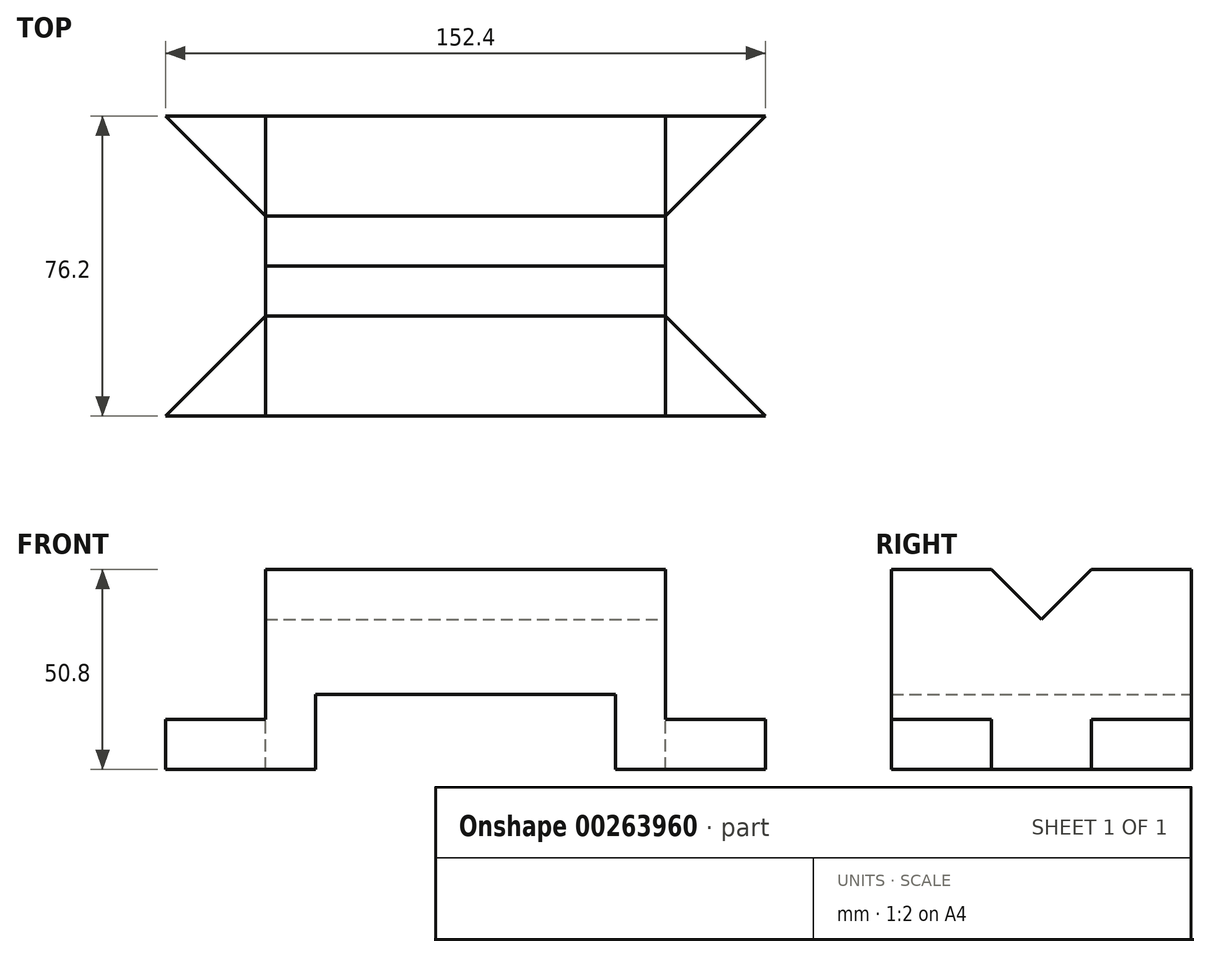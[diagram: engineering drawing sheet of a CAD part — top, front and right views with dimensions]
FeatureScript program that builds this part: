
annotation { "Feature Type Name" : "Feature", "Feature Type Description" : "" }
export const myFeature = defineFeature(function(context is Context, id is Id, definition is map)
    precondition{}
    {
        {
            var Q0;
            Q0=qCreatedBy(makeId("Front.planeOp"),FACE);
            var sketch = newSketch(context, id + "F0", { "sketchPlane" : qUnion([Q0])});
            skLineSegment(sketch, "E0", {"start": v(0, 0) * mm, "end": v(38.1, 0) * mm});
            skLineSegment(sketch, "E1", {"start": v(38.1, 0) * mm, "end": v(38.1, 19.05) * mm});
            skLineSegment(sketch, "E2", {"start": v(38.1, 19.05) * mm, "end": v(114.3, 19.05) * mm});
            skLineSegment(sketch, "E3", {"start": v(114.3, 19.05) * mm, "end": v(114.3, 0) * mm});
            skLineSegment(sketch, "E4", {"start": v(114.3, 0) * mm, "end": v(152.4, 0) * mm});
            skLineSegment(sketch, "E5", {"start": v(152.4, 0) * mm, "end": v(152.4, 12.7) * mm});
            skLineSegment(sketch, "E6", {"start": v(152.4, 12.7) * mm, "end": v(127, 12.7) * mm});
            skLineSegment(sketch, "E7", {"start": v(127, 12.7) * mm, "end": v(127, 50.8) * mm});
            skLineSegment(sketch, "E8", {"start": v(127, 50.8) * mm, "end": v(25.4, 50.8) * mm});
            skLineSegment(sketch, "E9", {"start": v(25.4, 50.8) * mm, "end": v(25.4, 12.7) * mm});
            skLineSegment(sketch, "E10", {"start": v(25.4, 12.7) * mm, "end": v(0, 12.7) * mm});
            skLineSegment(sketch, "E11", {"start": v(0, 12.7) * mm, "end": v(0, 0) * mm});
            skSolve(sketch);
        }
        {
            var Q0;
            Q0=makeQuery(id+"F0.imprint","IMPRINT",FACE,{"disambiguationData":[TD([[makeQuery(id+"F0.imprint","IMPRINT",EDGE,{"derivedFrom":sQuery(id+"F0.wireOp",EDGE,"E0")}),1.0]])]});
            extrude(context, id + "F1", {"entities" : qUnion([Q0]), "depth" : 76.2 * mm});
        }
        {
            var Q0;
            Q0=makeQuery(id+"F1.opExtrude","SWEPT_FACE",FACE,{"disambiguationData":[OSD([sQuery(id+"F0.wireOp",EDGE,"E6")])]});
            var sketch = newSketch(context, id + "F2", { "sketchPlane" : qUnion([Q0])});
            skLineSegment(sketch, "E12", {"start": v(127, -76.2) * mm, "end": v(127, -50.8) * mm, "construction": true});
            skLineSegment(sketch, "E13", {"start": v(127, -50.8) * mm, "end": v(152.4, -76.2) * mm});
            skLineSegment(sketch, "E14", {"start": v(152.4, -76.2) * mm, "end": v(152.4, 0) * mm});
            skLineSegment(sketch, "E15", {"start": v(152.4, 0) * mm, "end": v(127, -25.4) * mm});
            skLineSegment(sketch, "E16", {"start": v(127, -25.4) * mm, "end": v(127, 0) * mm, "construction": true});
            skSolve(sketch);
        }
        {
            var Q0;
            {var subQ0=sQuery(id+"F2.wireOp",EDGE,"E13");Q0=makeQuery(id+"F2.imprint","IMPRINT",FACE,{"disambiguationData":[TD([[makeQuery(id+"F2.imprint","IMPRINT",EDGE,{"derivedFrom":subQ0}),1.0]])]});}
            extrude(context, id + "F3", {"entities" : qUnion([Q0]), "operationType" : NewBodyOperationType.REMOVE, "oppositeDirection" : true, "depth" : 25.4 * mm});
        }
        {
            var Q0;
            Q0=makeQuery(id+"F1.opExtrude","SWEPT_FACE",FACE,{"disambiguationData":[OSD([sQuery(id+"F0.wireOp",EDGE,"E10")])]});
            var sketch = newSketch(context, id + "F4", { "sketchPlane" : qUnion([Q0])});
            skLineSegment(sketch, "E17", {"start": v(25.4, -76.2) * mm, "end": v(25.4, -50.8) * mm, "construction": true});
            skLineSegment(sketch, "E18", {"start": v(25.4, -50.8) * mm, "end": v(0, -76.2) * mm});
            skLineSegment(sketch, "E19", {"start": v(0, -76.2) * mm, "end": v(0, 0) * mm});
            skLineSegment(sketch, "E20", {"start": v(0, 0) * mm, "end": v(25.4, -25.4) * mm});
            skLineSegment(sketch, "E21", {"start": v(25.4, -25.4) * mm, "end": v(25.4, 0) * mm, "construction": true});
            skSolve(sketch);
        }
        {
            var Q0;
            {var subQ0=sQuery(id+"F4.wireOp",EDGE,"E18");Q0=makeQuery(id+"F4.imprint","IMPRINT",FACE,{"disambiguationData":[TD([[makeQuery(id+"F4.imprint","IMPRINT",EDGE,{"derivedFrom":subQ0}),-1.0]])]});}
            extrude(context, id + "F5", {"entities" : qUnion([Q0]), "operationType" : NewBodyOperationType.REMOVE, "oppositeDirection" : true, "depth" : 25.4 * mm});
        }
        {
            var Q0;
            {var subQ0=sQuery(id+"F0.wireOp",EDGE,"E7");Q0=makeQuery(id+"F3.boolean.opBoolean","MERGE",FACE,{"derivedFrom":[makeQuery(id+"F1.opExtrude","SWEPT_FACE",FACE,{"disambiguationData":[OSD([subQ0])]}),makeQuery(id+"F3.opExtrude","SWEPT_FACE",FACE,{"disambiguationData":[OSD([sQuery(id+"F0.wireOp",EDGE,"E6"),subQ0])]})]});}
            var sketch = newSketch(context, id + "F6", { "sketchPlane" : qUnion([Q0])});
            skLineSegment(sketch, "E22", {"start": v(-76.2, 50.8) * mm, "end": v(-76.2, 38.1) * mm, "construction": true});
            skLineSegment(sketch, "E23", {"start": v(-76.2, 38.1) * mm, "end": v(-38.1, 38.1) * mm, "construction": true});
            skLineSegment(sketch, "E24", {"start": v(-76.2, 50.8) * mm, "end": v(-50.8, 50.8) * mm, "construction": true});
            skLineSegment(sketch, "E25", {"start": v(-50.8, 50.8) * mm, "end": v(-38.1, 38.1) * mm});
            skLineSegment(sketch, "E26", {"start": v(-38.1, 50.8) * mm, "end": v(-38.1, 0) * mm, "construction": true});
            skLineSegment(sketch, "E27.MirrorCS", {"start": v(-25.4, 50.8) * mm, "end": v(-38.1, 38.1) * mm});
            skSolve(sketch);
        }
        {
            var Q0;
            {var subQ0=sQuery(id+"F6.wireOp",EDGE,"E25");Q0=makeQuery(id+"F6.imprint","IMPRINT",FACE,{"disambiguationData":[TD([[makeQuery(id+"F6.imprint","IMPRINT",EDGE,{"derivedFrom":subQ0}),1.0]])]});}
            extrude(context, id + "F7", {"entities" : qUnion([Q0]), "operationType" : NewBodyOperationType.REMOVE, "oppositeDirection" : true, "depth" : 101.6 * mm});
        }
    });
